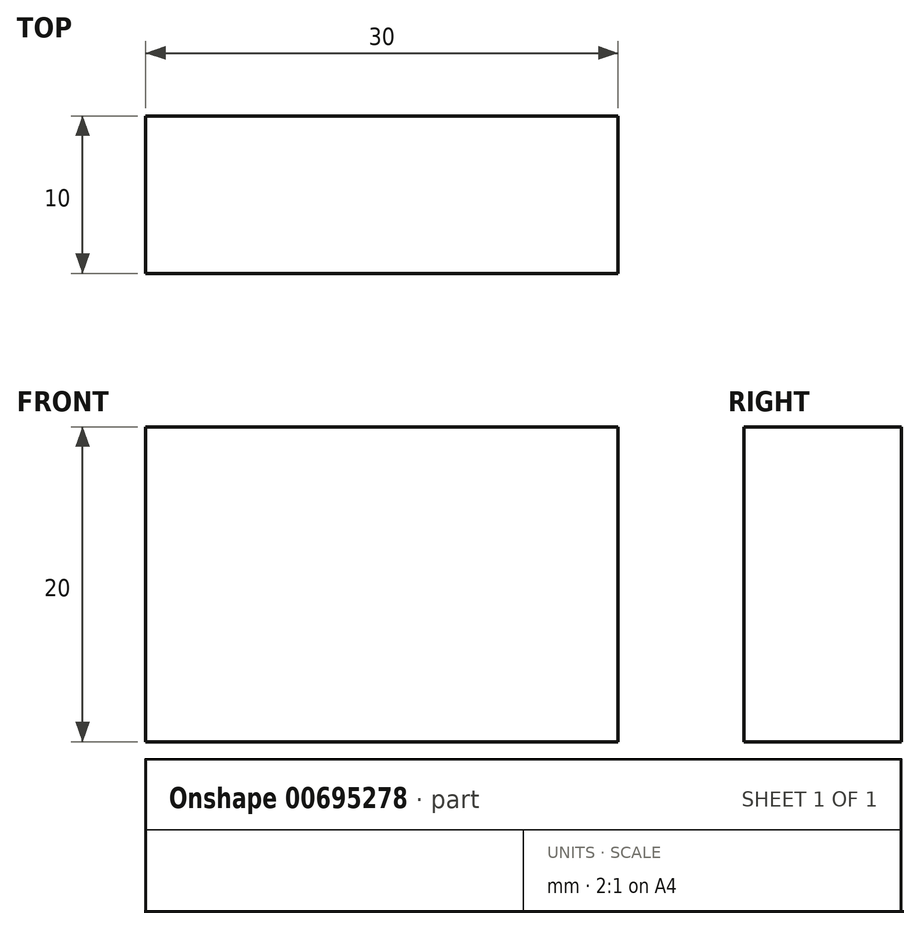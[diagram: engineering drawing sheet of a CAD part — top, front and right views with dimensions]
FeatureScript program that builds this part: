
annotation { "Feature Type Name" : "Feature", "Feature Type Description" : "" }
export const myFeature = defineFeature(function(context is Context, id is Id, definition is map)
    precondition{}
    {
        {
            var Q0;
            Q0=qCreatedBy(makeId("Top.planeOp"),FACE);
            var sketch = newSketch(context, id + "F0", { "sketchPlane" : qUnion([Q0])});
            skLineSegment(sketch, "E0.bottom", {"start": v(0, 0) * mm, "end": v(30, 0) * mm});
            skLineSegment(sketch, "E0.top", {"start": v(0, 10) * mm, "end": v(30, 10) * mm});
            skLineSegment(sketch, "E0.left", {"start": v(0, 0) * mm, "end": v(0, 10) * mm});
            skLineSegment(sketch, "E0.right", {"start": v(30, 0) * mm, "end": v(30, 10) * mm});
            skSolve(sketch);
        }
        {
            var Q0;
            Q0 = qSketchRegion(id + "F0", true);
            extrude(context, id + "F1", {"entities" : qUnion([Q0]), "oppositeDirection" : true, "depth" : 20 * mm, "offsetDistance" : 25 * mm});
        }
    });
